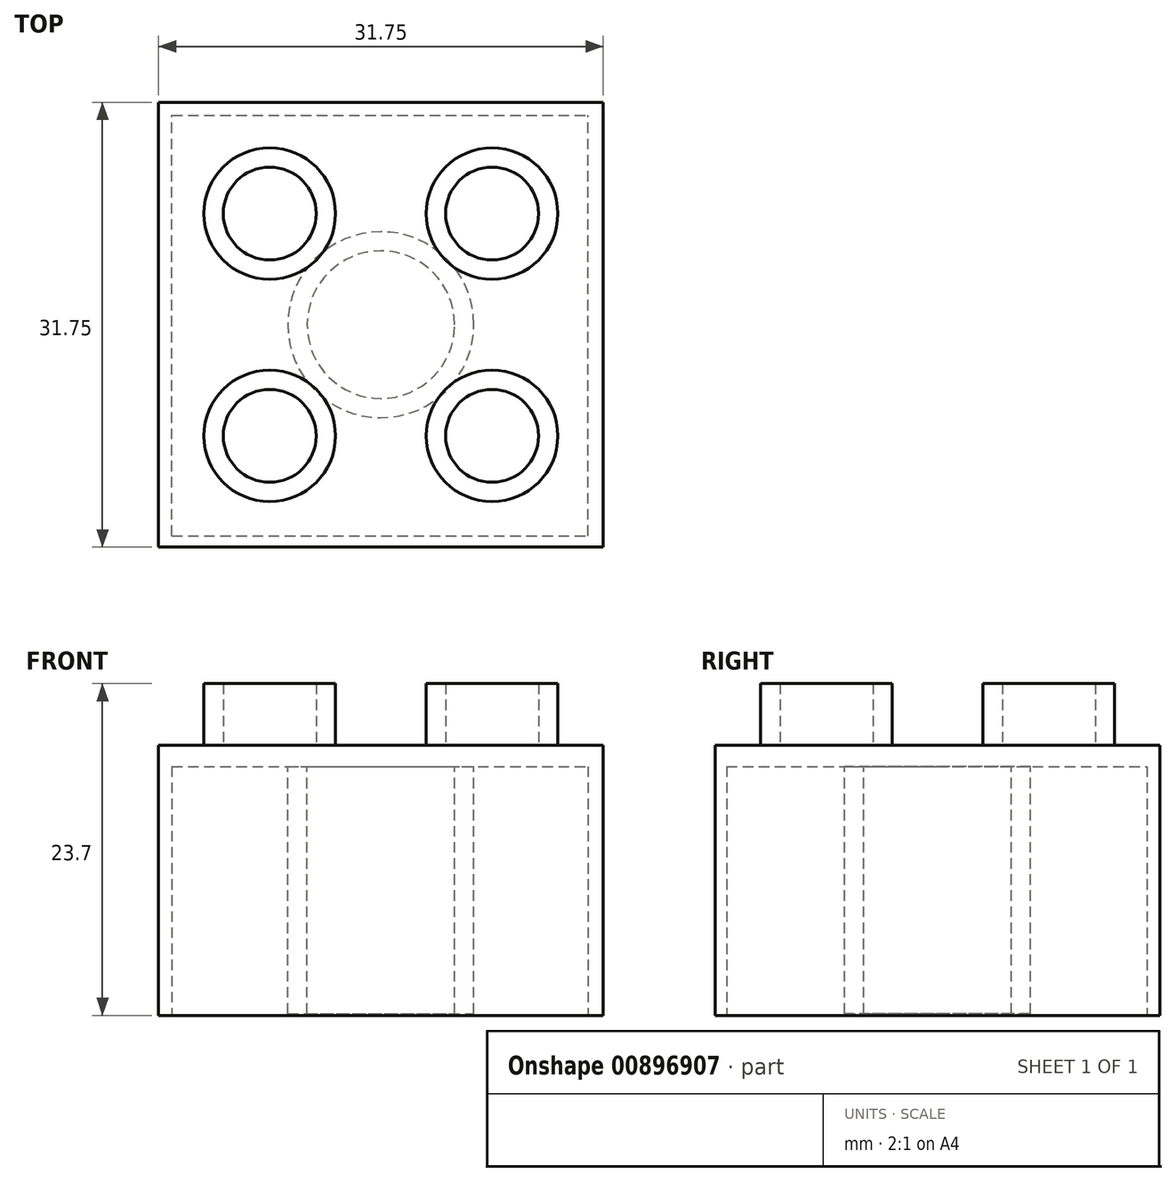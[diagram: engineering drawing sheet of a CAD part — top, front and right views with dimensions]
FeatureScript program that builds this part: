
annotation { "Feature Type Name" : "Feature", "Feature Type Description" : "" }
export const myFeature = defineFeature(function(context is Context, id is Id, definition is map)
    precondition{}
    {
        {
            var Q0;
            Q0=qCreatedBy(makeId("Top.planeOp"),FACE);
            var sketch = newSketch(context, id + "F0", { "sketchPlane" : qUnion([Q0])});
            skLineSegment(sketch, "E0.bottom", {"start": v(30.42, -36.97) * mm, "end": v(62.17, -36.97) * mm});
            skLineSegment(sketch, "E0.top", {"start": v(30.42, -68.72) * mm, "end": v(62.17, -68.72) * mm});
            skLineSegment(sketch, "E0.left", {"start": v(30.42, -36.97) * mm, "end": v(30.42, -68.72) * mm});
            skLineSegment(sketch, "E0.right", {"start": v(62.17, -36.97) * mm, "end": v(62.17, -68.72) * mm});
            skSolve(sketch);
        }
        {
            var Q0;
            Q0=makeQuery(id+"F0.imprint","IMPRINT",FACE,{"disambiguationData":[TD([[makeQuery(id+"F0.imprint","IMPRINT",EDGE,{"derivedFrom":sQuery(id+"F0.wireOp",EDGE,"E0.bottom")}),-1.0]])]});
            extrude(context, id + "F1", {"entities" : qUnion([Q0]), "depth" : 19.3 * mm, "offsetDistance" : 25.4 * mm});
        }
        {
            var Q0;
            Q0=makeQuery(id+"F1.opExtrude","CAP_FACE",FACE,{"disambiguationData":[OSD([sQuery(id+"F0.wireOp",EDGE,"E0.bottom"),sQuery(id+"F0.wireOp",EDGE,"E0.top"),sQuery(id+"F0.wireOp",EDGE,"E0.left"),sQuery(id+"F0.wireOp",EDGE,"E0.right")])],"isStart":false});
            var sketch = newSketch(context, id + "F2", { "sketchPlane" : qUnion([Q0])});
            skCircle(sketch, "E1", {"center": v(38.36, -44.9) * mm, "radius": 4.7 * mm});
            skCircle(sketch, "E2", {"center": v(38.36, -44.9) * mm, "radius": 3.31 * mm});
            skCircle(sketch, "E3", {"center": v(54.23, -44.9) * mm, "radius": 4.7 * mm});
            skCircle(sketch, "E4", {"center": v(54.23, -44.9) * mm, "radius": 3.31 * mm});
            skCircle(sketch, "E5", {"center": v(38.36, -60.78) * mm, "radius": 4.7 * mm});
            skCircle(sketch, "E6", {"center": v(38.36, -60.78) * mm, "radius": 3.31 * mm});
            skCircle(sketch, "E7", {"center": v(54.23, -60.78) * mm, "radius": 4.7 * mm});
            skCircle(sketch, "E8", {"center": v(54.23, -60.78) * mm, "radius": 3.31 * mm});
            skSolve(sketch);
        }
        {
            var Q0;
            Q0=makeQuery(id+"F2.imprint","IMPRINT",FACE,{"disambiguationData":[TD([[makeQuery(id+"F2.imprint","IMPRINT",EDGE,{"derivedFrom":sQuery(id+"F2.wireOp",EDGE,"E1")}),1.0]])]});
            var Q1;
            Q1=makeQuery(id+"F2.imprint","IMPRINT",FACE,{"disambiguationData":[TD([[makeQuery(id+"F2.imprint","IMPRINT",EDGE,{"derivedFrom":sQuery(id+"F2.wireOp",EDGE,"E3")}),1.0]])]});
            var Q2;
            Q2=makeQuery(id+"F2.imprint","IMPRINT",FACE,{"disambiguationData":[TD([[makeQuery(id+"F2.imprint","IMPRINT",EDGE,{"derivedFrom":sQuery(id+"F2.wireOp",EDGE,"E7")}),1.0]])]});
            var Q3;
            Q3=makeQuery(id+"F2.imprint","IMPRINT",FACE,{"disambiguationData":[TD([[makeQuery(id+"F2.imprint","IMPRINT",EDGE,{"derivedFrom":sQuery(id+"F2.wireOp",EDGE,"E5")}),1.0]])]});
            extrude(context, id + "F3", {"entities" : qUnion([Q0, Q1, Q2, Q3]), "operationType" : NewBodyOperationType.ADD, "depth" : 4.4 * mm, "offsetDistance" : 25.4 * mm});
        }
        {
            var Q0;
            Q0=makeQuery(id+"F1.opExtrude","CAP_FACE",FACE,{"disambiguationData":[OSD([sQuery(id+"F0.wireOp",EDGE,"E0.bottom"),sQuery(id+"F0.wireOp",EDGE,"E0.top"),sQuery(id+"F0.wireOp",EDGE,"E0.left"),sQuery(id+"F0.wireOp",EDGE,"E0.right")])],"isStart":true});
            var sketch = newSketch(context, id + "F4", { "sketchPlane" : qUnion([Q0])});
            skLineSegment(sketch, "E9.bottom", {"start": v(31.38, 67.91) * mm, "end": v(61.09, 67.91) * mm});
            skLineSegment(sketch, "E9.top", {"start": v(31.38, 37.9) * mm, "end": v(61.09, 37.9) * mm});
            skLineSegment(sketch, "E9.left", {"start": v(31.38, 67.91) * mm, "end": v(31.38, 37.9) * mm});
            skLineSegment(sketch, "E9.right", {"start": v(61.09, 67.91) * mm, "end": v(61.09, 37.9) * mm});
            skSolve(sketch);
        }
        {
            var Q0;
            Q0=makeQuery(id+"F4.imprint","IMPRINT",FACE,{"disambiguationData":[TD([[makeQuery(id+"F4.imprint","IMPRINT",EDGE,{"derivedFrom":sQuery(id+"F4.wireOp",EDGE,"E9.bottom")}),-1.0]])]});
            extrude(context, id + "F5", {"entities" : qUnion([Q0]), "operationType" : NewBodyOperationType.REMOVE, "oppositeDirection" : true, "depth" : 17.78 * mm, "offsetDistance" : 25.4 * mm});
        }
        {
            var Q0;
            Q0=makeQuery(id+"F5.boolean.opBoolean","COPY",FACE,{"derivedFrom":makeQuery(id+"F5.opExtrude","CAP_FACE",FACE,{"disambiguationData":[OSD([sQuery(id+"F4.wireOp",EDGE,"E9.bottom"),sQuery(id+"F4.wireOp",EDGE,"E9.top"),sQuery(id+"F4.wireOp",EDGE,"E9.left"),sQuery(id+"F4.wireOp",EDGE,"E9.right")])],"isStart":false})});
            var sketch = newSketch(context, id + "F6", { "sketchPlane" : qUnion([Q0])});
            skSolve(sketch);
        }
        {
            var Q0;
            Q0=makeQuery(id+"F6.imprint","IMPRINT",FACE,{"disambiguationData":[TD([[makeQuery(id+"F6.imprint","IMPRINT",EDGE,{"derivedFrom":makeQuery(id+"F5.boolean.opBoolean","COPY",EDGE,{"derivedFrom":makeQuery(id+"F5.opExtrude","CAP_EDGE",EDGE,{"disambiguationData":[OSD([sQuery(id+"F4.wireOp",EDGE,"E9.bottom")])],"isStart":false})})}),-1.0]])]});
            var sketch = newSketch(context, id + "F7", { "sketchPlane" : qUnion([Q0])});
            skCircle(sketch, "E10", {"center": v(46.3, 52.84) * mm, "radius": 6.64 * mm});
            skCircle(sketch, "E11", {"center": v(46.3, 52.84) * mm, "radius": 5.27 * mm});
            skSolve(sketch);
        }
        {
            var Q0;
            Q0 = qSketchRegion(id + "F6", true);
            var Q1;
            Q1 = qSketchRegion(id + "F7", true);
            extrude(context, id + "F8", {"entities" : qUnion([Q0, Q1]), "operationType" : NewBodyOperationType.ADD, "depth" : 17.65 * mm, "offsetDistance" : 25.4 * mm});
        }
    });
